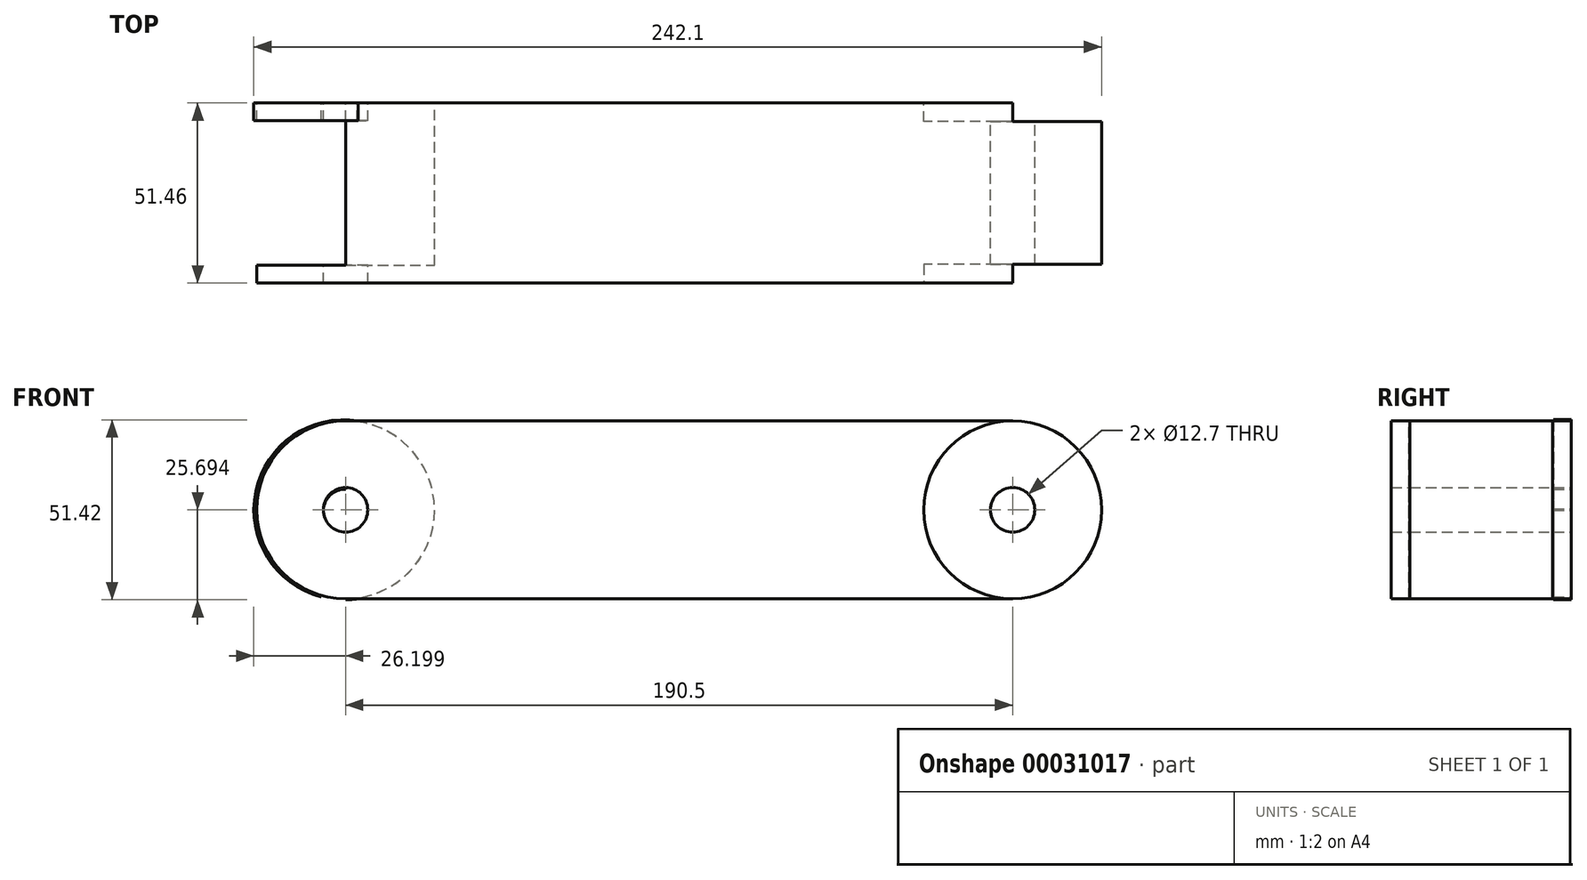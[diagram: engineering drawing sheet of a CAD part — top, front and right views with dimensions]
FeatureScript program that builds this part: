
annotation { "Feature Type Name" : "Feature", "Feature Type Description" : "" }
export const myFeature = defineFeature(function(context is Context, id is Id, definition is map)
    precondition{}
    {
        {
            var Q0;
            Q0=qCreatedBy(makeId("Front.planeOp"),FACE);
            var sketch = newSketch(context, id + "F0", { "sketchPlane" : qUnion([Q0])});
            skCircle(sketch, "E0", {"center": v(-70.17, -28.9) * mm, "radius": 25.4 * mm});
            skLineSegment(sketch, "E1.bottom", {"start": v(-70.17, -3.5) * mm, "end": v(120.33, -3.5) * mm});
            skLineSegment(sketch, "E1.top", {"start": v(-70.17, -54.3) * mm, "end": v(120.33, -54.3) * mm});
            skLineSegment(sketch, "E1.left", {"start": v(-70.17, -3.5) * mm, "end": v(-70.17, -54.3) * mm});
            skLineSegment(sketch, "E1.right", {"start": v(120.33, -3.5) * mm, "end": v(120.33, -54.3) * mm});
            skCircle(sketch, "E2", {"center": v(120.33, -28.9) * mm, "radius": 25.4 * mm});
            skCircle(sketch, "E3", {"center": v(-70.17, -28.9) * mm, "radius": 6.35 * mm});
            skCircle(sketch, "E4", {"center": v(120.33, -28.9) * mm, "radius": 6.35 * mm});
            skSolve(sketch);
        }
        {
            var Q0;
            {var subQ0=sQuery(id+"F0.wireOp",EDGE,"E3");var subQ1=sQuery(id+"F0.wireOp",EDGE,"E1.left");var subQ3=makeQuery(id+"F0.imprint","INTERSECT",VERTEX,{"disambiguationData":[OD(0.0)],"derivedFrom":[subQ1,subQ0]});Q0=makeQuery(id+"F0.imprint","IMPRINT",FACE,{"disambiguationData":[TD([[makeQuery(id+"F0.imprint","IMPRINT",EDGE,{"disambiguationData":[TD([[subQ3,1.0]])],"derivedFrom":subQ0}),-1.0]])]});}
            var Q1;
            {var subQ0=sQuery(id+"F0.wireOp",EDGE,"E3");var subQ1=sQuery(id+"F0.wireOp",EDGE,"E1.left");var subQ3=makeQuery(id+"F0.imprint","INTERSECT",VERTEX,{"disambiguationData":[OD(0.0)],"derivedFrom":[subQ1,subQ0]});Q1=makeQuery(id+"F0.imprint","IMPRINT",FACE,{"disambiguationData":[TD([[makeQuery(id+"F0.imprint","IMPRINT",EDGE,{"disambiguationData":[TD([[subQ3,-1.0]])],"derivedFrom":subQ0}),-1.0]])]});}
            var Q2;
            {var subQ3=sQuery(id+"F0.wireOp",EDGE,"E1.bottom");Q2=makeQuery(id+"F0.imprint","IMPRINT",FACE,{"disambiguationData":[TD([[makeQuery(id+"F0.imprint","IMPRINT",EDGE,{"derivedFrom":subQ3}),-1.0]])]});}
            var Q3;
            {var subQ0=sQuery(id+"F0.wireOp",EDGE,"E4");var subQ1=sQuery(id+"F0.wireOp",EDGE,"E1.right");var subQ3=makeQuery(id+"F0.imprint","INTERSECT",VERTEX,{"disambiguationData":[OD(0.0)],"derivedFrom":[subQ1,subQ0]});Q3=makeQuery(id+"F0.imprint","IMPRINT",FACE,{"disambiguationData":[TD([[makeQuery(id+"F0.imprint","IMPRINT",EDGE,{"disambiguationData":[TD([[subQ3,-1.0]])],"derivedFrom":subQ0}),-1.0]])]});}
            var Q4;
            {var subQ0=sQuery(id+"F0.wireOp",EDGE,"E4");var subQ1=sQuery(id+"F0.wireOp",EDGE,"E1.right");var subQ3=makeQuery(id+"F0.imprint","INTERSECT",VERTEX,{"disambiguationData":[OD(0.0)],"derivedFrom":[subQ1,subQ0]});Q4=makeQuery(id+"F0.imprint","IMPRINT",FACE,{"disambiguationData":[TD([[makeQuery(id+"F0.imprint","IMPRINT",EDGE,{"disambiguationData":[TD([[subQ3,1.0]])],"derivedFrom":subQ0}),-1.0]])]});}
            extrude(context, id + "F1", {"entities" : qUnion([Q0, Q1, Q2, Q3, Q4]), "depth" : 51.46 * mm});
        }
        {
            var Q0;
            {var subQ0=sQuery(id+"F0.wireOp",EDGE,"E4");var subQ1=sQuery(id+"F0.wireOp",EDGE,"E1.right");var subQ3=makeQuery(id+"F0.imprint","INTERSECT",VERTEX,{"disambiguationData":[OD(0.0)],"derivedFrom":[subQ1,subQ0]});Q0=makeQuery(id+"F0.imprint","IMPRINT",FACE,{"disambiguationData":[TD([[makeQuery(id+"F0.imprint","IMPRINT",EDGE,{"disambiguationData":[TD([[subQ3,1.0]])],"derivedFrom":subQ0}),-1.0]])]});}
            var Q1;
            {var subQ0=sQuery(id+"F0.wireOp",EDGE,"E4");var subQ1=sQuery(id+"F0.wireOp",EDGE,"E1.right");var subQ3=makeQuery(id+"F0.imprint","INTERSECT",VERTEX,{"disambiguationData":[OD(0.0)],"derivedFrom":[subQ1,subQ0]});Q1=makeQuery(id+"F0.imprint","IMPRINT",FACE,{"disambiguationData":[TD([[makeQuery(id+"F0.imprint","IMPRINT",EDGE,{"disambiguationData":[TD([[subQ3,-1.0]])],"derivedFrom":subQ0}),-1.0]])]});}
            extrude(context, id + "F2", {"entities" : qUnion([Q0, Q1]), "operationType" : NewBodyOperationType.REMOVE, "depth" : 5.33 * mm});
        }
        {
            var Q0;
            Q0=makeQuery(id+"F1.opExtrude","CAP_FACE",FACE,{"disambiguationData":[OSD([sQuery(id+"F0.wireOp",EDGE,"E0"),sQuery(id+"F0.wireOp",EDGE,"E1.bottom"),sQuery(id+"F0.wireOp",EDGE,"E1.top"),sQuery(id+"F0.wireOp",EDGE,"E2"),sQuery(id+"F0.wireOp",EDGE,"E3"),sQuery(id+"F0.wireOp",EDGE,"E4")])],"isStart":false});
            var sketch = newSketch(context, id + "F3", { "sketchPlane" : qUnion([Q0])});
            skCircle(sketch, "E5", {"center": v(120.33, -28.9) * mm, "radius": 25.4 * mm});
            skCircle(sketch, "E6", {"center": v(-70.17, -28.9) * mm, "radius": 25.4 * mm});
            skSolve(sketch);
        }
        {
            var Q0;
            Q0=makeQuery(id+"F3.imprint","IMPRINT",FACE,{"disambiguationData":[TD([[makeQuery(id+"F3.imprint","IMPRINT",EDGE,{"derivedFrom":makeQuery(id+"F1.opExtrude","CAP_EDGE",EDGE,{"disambiguationData":[OSD([sQuery(id+"F0.wireOp",EDGE,"E4")])],"isStart":false})}),-1.0]])]});
            extrude(context, id + "F4", {"entities" : qUnion([Q0]), "operationType" : NewBodyOperationType.REMOVE, "oppositeDirection" : true, "depth" : 5.33 * mm});
        }
        {
            var Q0;
            {var subQ0=sQuery(id+"F0.wireOp",EDGE,"E3");var subQ1=sQuery(id+"F0.wireOp",EDGE,"E1.left");var subQ3=makeQuery(id+"F0.imprint","INTERSECT",VERTEX,{"disambiguationData":[OD(0.0)],"derivedFrom":[subQ1,subQ0]});Q0=makeQuery(id+"F0.imprint","IMPRINT",FACE,{"disambiguationData":[TD([[makeQuery(id+"F0.imprint","IMPRINT",EDGE,{"disambiguationData":[TD([[subQ3,1.0]])],"derivedFrom":subQ0}),-1.0]])]});}
            var Q1;
            {var subQ0=sQuery(id+"F0.wireOp",EDGE,"E3");var subQ1=sQuery(id+"F0.wireOp",EDGE,"E1.left");var subQ3=makeQuery(id+"F0.imprint","INTERSECT",VERTEX,{"disambiguationData":[OD(0.0)],"derivedFrom":[subQ1,subQ0]});Q1=makeQuery(id+"F0.imprint","IMPRINT",FACE,{"disambiguationData":[TD([[makeQuery(id+"F0.imprint","IMPRINT",EDGE,{"disambiguationData":[TD([[subQ3,-1.0]])],"derivedFrom":subQ0}),-1.0]])]});}
            extrude(context, id + "F5", {"entities" : qUnion([Q0, Q1]), "operationType" : NewBodyOperationType.REMOVE, "depth" : 46.38 * mm});
        }
        {
            var Q0;
            {var subQ3=sQuery(id+"F0.wireOp",EDGE,"E1.bottom");Q0=makeQuery(id+"F0.imprint","IMPRINT",FACE,{"disambiguationData":[TD([[makeQuery(id+"F0.imprint","IMPRINT",EDGE,{"derivedFrom":subQ3}),-1.0]])]});}
            var sketch = newSketch(context, id + "F6", { "sketchPlane" : qUnion([Q0])});
            skLineSegment(sketch, "E7.bottom", {"start": v(0, -3.18) * mm, "end": v(-70.66, -3.18) * mm});
            skLineSegment(sketch, "E7.top", {"start": v(0, -54.6) * mm, "end": v(-70.66, -54.6) * mm});
            skLineSegment(sketch, "E7.left", {"start": v(0, -3.18) * mm, "end": v(0, -54.6) * mm});
            skLineSegment(sketch, "E7.right", {"start": v(-70.66, -3.18) * mm, "end": v(-70.66, -54.6) * mm});
            skCircle(sketch, "E8", {"center": v(-70.66, -28.89) * mm, "radius": 25.71 * mm});
            skSolve(sketch);
        }
        {
            var Q0;
            {var subQ3=sQuery(id+"F0.wireOp",EDGE,"E1.bottom");Q0=makeQuery(id+"F0.imprint","IMPRINT",FACE,{"disambiguationData":[TD([[makeQuery(id+"F0.imprint","IMPRINT",EDGE,{"derivedFrom":subQ3}),-1.0]])]});}
            var sketch = newSketch(context, id + "F7", { "sketchPlane" : qUnion([Q0])});
            skLineSegment(sketch, "E9.bottom", {"start": v(-70.18, -54.74) * mm, "end": v(120.32, -54.74) * mm});
            skLineSegment(sketch, "E9.top", {"start": v(-70.18, -3.94) * mm, "end": v(120.32, -3.94) * mm});
            skLineSegment(sketch, "E9.left", {"start": v(-70.18, -54.74) * mm, "end": v(-70.18, -3.94) * mm});
            skLineSegment(sketch, "E9.right", {"start": v(120.32, -54.74) * mm, "end": v(120.32, -3.94) * mm});
            skCircle(sketch, "E10", {"center": v(-70.18, -29.34) * mm, "radius": 25.4 * mm});
            skCircle(sketch, "E11", {"center": v(-70.18, -29.34) * mm, "radius": 6.35 * mm});
            skSolve(sketch);
        }
        {
            var Q0;
            {var subQ1=sQuery(id+"F6.wireOp",EDGE,"E7.right");Q0=makeQuery(id+"F6.imprint","IMPRINT",FACE,{"disambiguationData":[TD([[makeQuery(id+"F6.imprint","IMPRINT",EDGE,{"derivedFrom":subQ1}),-1.0]])]});}
            var Q1;
            {var subQ14=sQuery(id+"F6.wireOp",EDGE,"E7.right");Q1=makeQuery(id+"F6.imprint","IMPRINT",FACE,{"disambiguationData":[TD([[makeQuery(id+"F6.imprint","IMPRINT",EDGE,{"derivedFrom":subQ14}),1.0]])]});}
            extrude(context, id + "F8", {"entities" : qUnion([Q0, Q1]), "operationType" : NewBodyOperationType.ADD, "depth" : 5.08 * mm});
        }
        {
            var Q0;
            {var subQ0=sQuery(id+"F7.wireOp",EDGE,"E11");var subQ1=sQuery(id+"F7.wireOp",EDGE,"E9.left");var subQ3=makeQuery(id+"F7.imprint","INTERSECT",VERTEX,{"disambiguationData":[OD(0.0)],"derivedFrom":[subQ1,subQ0]});Q0=makeQuery(id+"F7.imprint","IMPRINT",FACE,{"disambiguationData":[TD([[makeQuery(id+"F7.imprint","IMPRINT",EDGE,{"disambiguationData":[TD([[subQ3,-1.0]])],"derivedFrom":subQ1}),1.0]])]});}
            var Q1;
            {var subQ0=sQuery(id+"F0.wireOp",EDGE,"E3");var subQ1=sQuery(id+"F0.wireOp",EDGE,"E1.left");var subQ3=makeQuery(id+"F0.imprint","INTERSECT",VERTEX,{"disambiguationData":[OD(0.0)],"derivedFrom":[subQ1,subQ0]});Q1=makeQuery(id+"F0.imprint","IMPRINT",FACE,{"disambiguationData":[TD([[makeQuery(id+"F0.imprint","IMPRINT",EDGE,{"disambiguationData":[TD([[subQ3,-1.0]])],"derivedFrom":subQ1}),1.0]])]});}
            extrude(context, id + "F9", {"entities" : qUnion([Q0, Q1]), "operationType" : NewBodyOperationType.REMOVE, "depth" : 28.86 * mm});
        }
        {
            var Q0;
            {var subQ0=sQuery(id+"F0.wireOp",EDGE,"E3");var subQ1=sQuery(id+"F0.wireOp",EDGE,"E1.left");var subQ3=makeQuery(id+"F0.imprint","INTERSECT",VERTEX,{"disambiguationData":[OD(0.0)],"derivedFrom":[subQ1,subQ0]});Q0=makeQuery(id+"F0.imprint","IMPRINT",FACE,{"disambiguationData":[TD([[makeQuery(id+"F0.imprint","IMPRINT",EDGE,{"disambiguationData":[TD([[subQ3,-1.0]])],"derivedFrom":subQ1}),-1.0]])]});}
            extrude(context, id + "F10", {"entities" : qUnion([Q0]), "operationType" : NewBodyOperationType.REMOVE, "depth" : 31.25 * mm});
        }
    });
